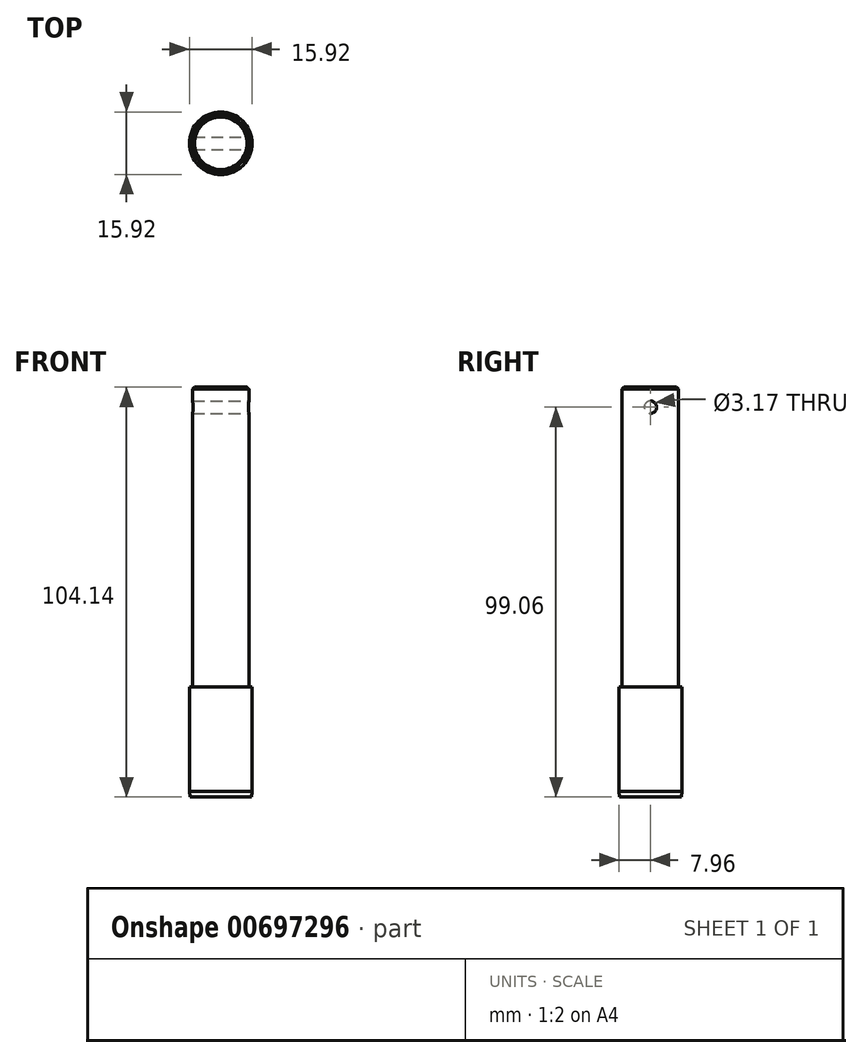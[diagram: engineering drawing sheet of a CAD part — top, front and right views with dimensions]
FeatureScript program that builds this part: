
annotation { "Feature Type Name" : "Feature", "Feature Type Description" : "" }
export const myFeature = defineFeature(function(context is Context, id is Id, definition is map)
    precondition{}
    {
        {
            var Q0;
            Q0=qCreatedBy(makeId("Top.planeOp"),FACE);
            var sketch = newSketch(context, id + "F0", { "sketchPlane" : qUnion([Q0])});
            skCircle(sketch, "E0", {"center": v(0, 0) * mm, "radius": 7.96 * mm});
            skSolve(sketch);
        }
        {
            var Q0;
            Q0=makeQuery(id+"F0.imprint","IMPRINT",FACE,{"disambiguationData":[TD([[makeQuery(id+"F0.imprint","IMPRINT",EDGE,{"derivedFrom":sQuery(id+"F0.wireOp",EDGE,"E0")}),1.0]])]});
            extrude(context, id + "F1", {"entities" : qUnion([Q0]), "depth" : 27.94 * mm, "offsetDistance" : 25.4 * mm});
        }
        {
            var Q0;
            Q0=makeQuery(id+"F1.opExtrude","CAP_FACE",FACE,{"disambiguationData":[OSD([sQuery(id+"F0.wireOp",EDGE,"E0")])],"isStart":false});
            var sketch = newSketch(context, id + "F2", { "sketchPlane" : qUnion([Q0])});
            skCircle(sketch, "E1", {"center": v(0, 0) * mm, "radius": 7.18 * mm});
            skSolve(sketch);
        }
        {
            var Q0;
            Q0=makeQuery(id+"F2.imprint","IMPRINT",FACE,{"disambiguationData":[TD([[makeQuery(id+"F2.imprint","IMPRINT",EDGE,{"derivedFrom":sQuery(id+"F2.wireOp",EDGE,"E1")}),1.0]])]});
            extrude(context, id + "F3", {"entities" : qUnion([Q0]), "operationType" : NewBodyOperationType.ADD, "depth" : 76.2 * mm, "offsetDistance" : 25.4 * mm});
        }
        {
            var Q0;
            Q0=makeQuery(id+"F3.opExtrude","CAP_EDGE",EDGE,{"disambiguationData":[OSD([sQuery(id+"F2.wireOp",EDGE,"E1")])],"isStart":false});
            cPlane(context, id + "F4", {"entities" : qUnion([Q0]), "cplaneType" : CPlaneType.LINE_ANGLE, "offset" : 25.4 * mm, "angle" : 0 * degree, "width" : 152.4 * mm, "height" : 152.4 * mm});
        }
        {
            var Q0;
            Q0=qCreatedBy(id+"F4.planeOp",FACE);
            var sketch = newSketch(context, id + "F5", { "sketchPlane" : qUnion([Q0])});
            skCircle(sketch, "E2", {"center": v(0, 99.06) * mm, "radius": 1.59 * mm});
            skSolve(sketch);
        }
        {
            var Q0;
            Q0 = qSketchRegion(id + "F5", true);
            extrude(context, id + "F6", {"entities" : qUnion([Q0]), "operationType" : NewBodyOperationType.REMOVE, "endBound" : BoundingType.SYMMETRIC, "oppositeDirection" : true, "depth" : 25.4 * mm, "offsetDistance" : 25.4 * mm});
        }
        {
            var Q0;
            Q0=makeQuery(id+"F3.opExtrude","CAP_EDGE",EDGE,{"disambiguationData":[OSD([sQuery(id+"F2.wireOp",EDGE,"E1")])],"isStart":false});
            chamfer(context, id + "F7", {"entities" : qUnion([Q0]), "width" : 0.5 * mm, "tangentPropagation" : true});
        }
        {
            var Q0;
            Q0=makeQuery(id+"F1.opExtrude","CAP_EDGE",EDGE,{"disambiguationData":[OSD([sQuery(id+"F0.wireOp",EDGE,"E0")])],"isStart":true});
            chamfer(context, id + "F8", {"entities" : qUnion([Q0]), "chamferType" : ChamferType.OFFSET_ANGLE, "width" : 0.13 * mm, "oppositeDirection" : true, "angle" : 85 * degree, "tangentPropagation" : true});
        }
    });
